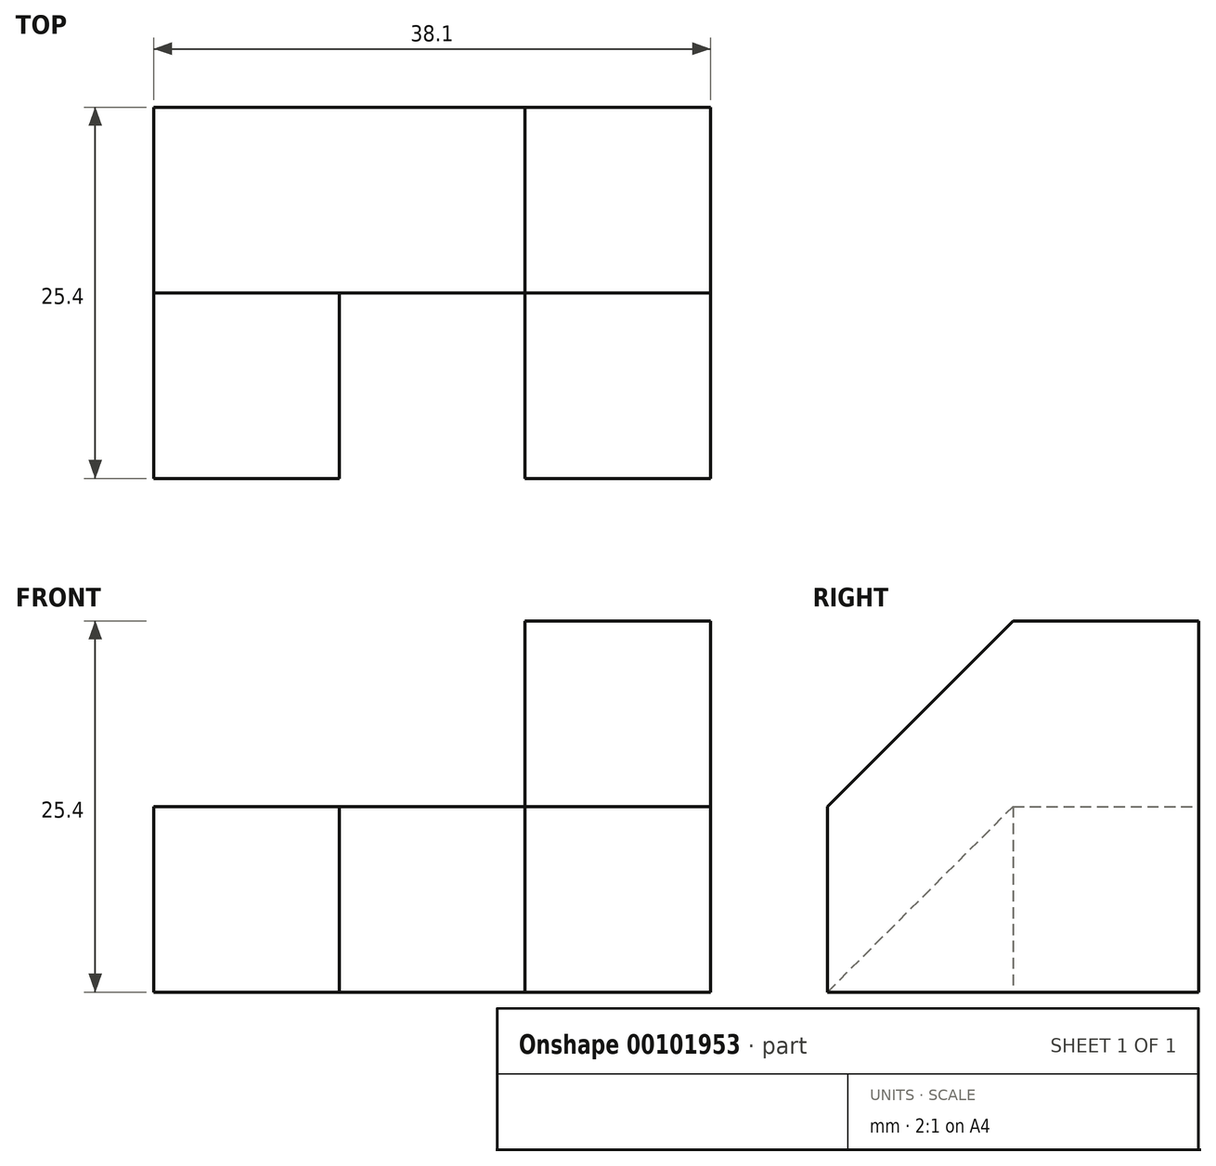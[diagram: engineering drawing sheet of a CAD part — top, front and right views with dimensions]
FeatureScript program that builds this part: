
annotation { "Feature Type Name" : "Feature", "Feature Type Description" : "" }
export const myFeature = defineFeature(function(context is Context, id is Id, definition is map)
    precondition{}
    {
        {
            var Q0;
            Q0=qCreatedBy(makeId("Right.planeOp"),FACE);
            var sketch = newSketch(context, id + "F0", { "sketchPlane" : qUnion([Q0])});
            skLineSegment(sketch, "E0", {"start": v(0, 0) * mm, "end": v(0, 12.7) * mm});
            skLineSegment(sketch, "E1", {"start": v(0, 12.7) * mm, "end": v(12.7, 25.4) * mm});
            skLineSegment(sketch, "E2", {"start": v(12.7, 25.4) * mm, "end": v(25.4, 25.4) * mm});
            skLineSegment(sketch, "E3", {"start": v(25.4, 25.4) * mm, "end": v(25.4, 0) * mm});
            skLineSegment(sketch, "E4", {"start": v(25.4, 0) * mm, "end": v(0, 0) * mm});
            skSolve(sketch);
        }
        {
            var Q0;
            Q0=makeQuery(id+"F0.imprint","IMPRINT",FACE,{"disambiguationData":[TD([[makeQuery(id+"F0.imprint","IMPRINT",EDGE,{"derivedFrom":sQuery(id+"F0.wireOp",EDGE,"E0")}),-1.0]])]});
            extrude(context, id + "F1", {"entities" : qUnion([Q0]), "oppositeDirection" : true, "depth" : 38.1 * mm});
        }
        {
            var Q0;
            Q0=makeQuery(id+"F1.opExtrude","SWEPT_FACE",FACE,{"disambiguationData":[OSD([sQuery(id+"F0.wireOp",EDGE,"E3")])]});
            var sketch = newSketch(context, id + "F2", { "sketchPlane" : qUnion([Q0])});
            skLineSegment(sketch, "E5.bottom", {"start": v(38.1, 25.4) * mm, "end": v(12.7, 25.4) * mm});
            skLineSegment(sketch, "E5.top", {"start": v(38.1, 12.7) * mm, "end": v(12.7, 12.7) * mm});
            skLineSegment(sketch, "E5.left", {"start": v(38.1, 25.4) * mm, "end": v(38.1, 12.7) * mm});
            skLineSegment(sketch, "E5.right", {"start": v(12.7, 25.4) * mm, "end": v(12.7, 12.7) * mm});
            skSolve(sketch);
        }
        {
            var Q0;
            Q0=makeQuery(id+"F2.imprint","IMPRINT",FACE,{"disambiguationData":[TD([[makeQuery(id+"F2.imprint","IMPRINT",EDGE,{"derivedFrom":sQuery(id+"F2.wireOp",EDGE,"E5.bottom")}),1.0]])]});
            extrude(context, id + "F3", {"entities" : qUnion([Q0]), "operationType" : NewBodyOperationType.REMOVE, "oppositeDirection" : true, "depth" : 25.4 * mm});
        }
        {
            var Q0;
            Q0=makeQuery(id+"F1.opExtrude","SWEPT_FACE",FACE,{"disambiguationData":[OSD([sQuery(id+"F0.wireOp",EDGE,"E0")])]});
            var sketch = newSketch(context, id + "F4", { "sketchPlane" : qUnion([Q0])});
            skLineSegment(sketch, "E6.bottom", {"start": v(-12.7, 12.7) * mm, "end": v(-25.4, 12.7) * mm});
            skLineSegment(sketch, "E6.top", {"start": v(-12.7, 0) * mm, "end": v(-25.4, 0) * mm});
            skLineSegment(sketch, "E6.left", {"start": v(-12.7, 12.7) * mm, "end": v(-12.7, 0) * mm});
            skLineSegment(sketch, "E6.right", {"start": v(-25.4, 12.7) * mm, "end": v(-25.4, 0) * mm});
            skSolve(sketch);
        }
        {
            var Q0;
            Q0 = qSketchRegion(id + "F4", true);
            extrude(context, id + "F5", {"entities" : qUnion([Q0]), "operationType" : NewBodyOperationType.REMOVE, "oppositeDirection" : true, "depth" : 12.7 * mm});
        }
        {
            var Q0;
            Q0=makeQuery(id+"F1.opExtrude","CAP_FACE",FACE,{"disambiguationData":[OSD([sQuery(id+"F0.wireOp",EDGE,"E0"),sQuery(id+"F0.wireOp",EDGE,"E1"),sQuery(id+"F0.wireOp",EDGE,"E2"),sQuery(id+"F0.wireOp",EDGE,"E3"),sQuery(id+"F0.wireOp",EDGE,"E4")])],"isStart":false});
            var sketch = newSketch(context, id + "F6", { "sketchPlane" : qUnion([Q0])});
            skLineSegment(sketch, "E7", {"start": v(0, 0) * mm, "end": v(-12.7, 12.7) * mm});
            skLineSegment(sketch, "E8", {"start": v(-12.7, 12.7) * mm, "end": v(0, 12.7) * mm});
            skLineSegment(sketch, "E9", {"start": v(0, 12.7) * mm, "end": v(0, 0) * mm});
            skSolve(sketch);
        }
        {
            var Q0;
            Q0=makeQuery(id+"F6.imprint","IMPRINT",FACE,{"disambiguationData":[TD([[makeQuery(id+"F6.imprint","IMPRINT",EDGE,{"derivedFrom":sQuery(id+"F6.wireOp",EDGE,"E7")}),-1.0]])]});
            extrude(context, id + "F7", {"entities" : qUnion([Q0]), "operationType" : NewBodyOperationType.REMOVE, "oppositeDirection" : true, "depth" : 12.7 * mm});
        }
    });
